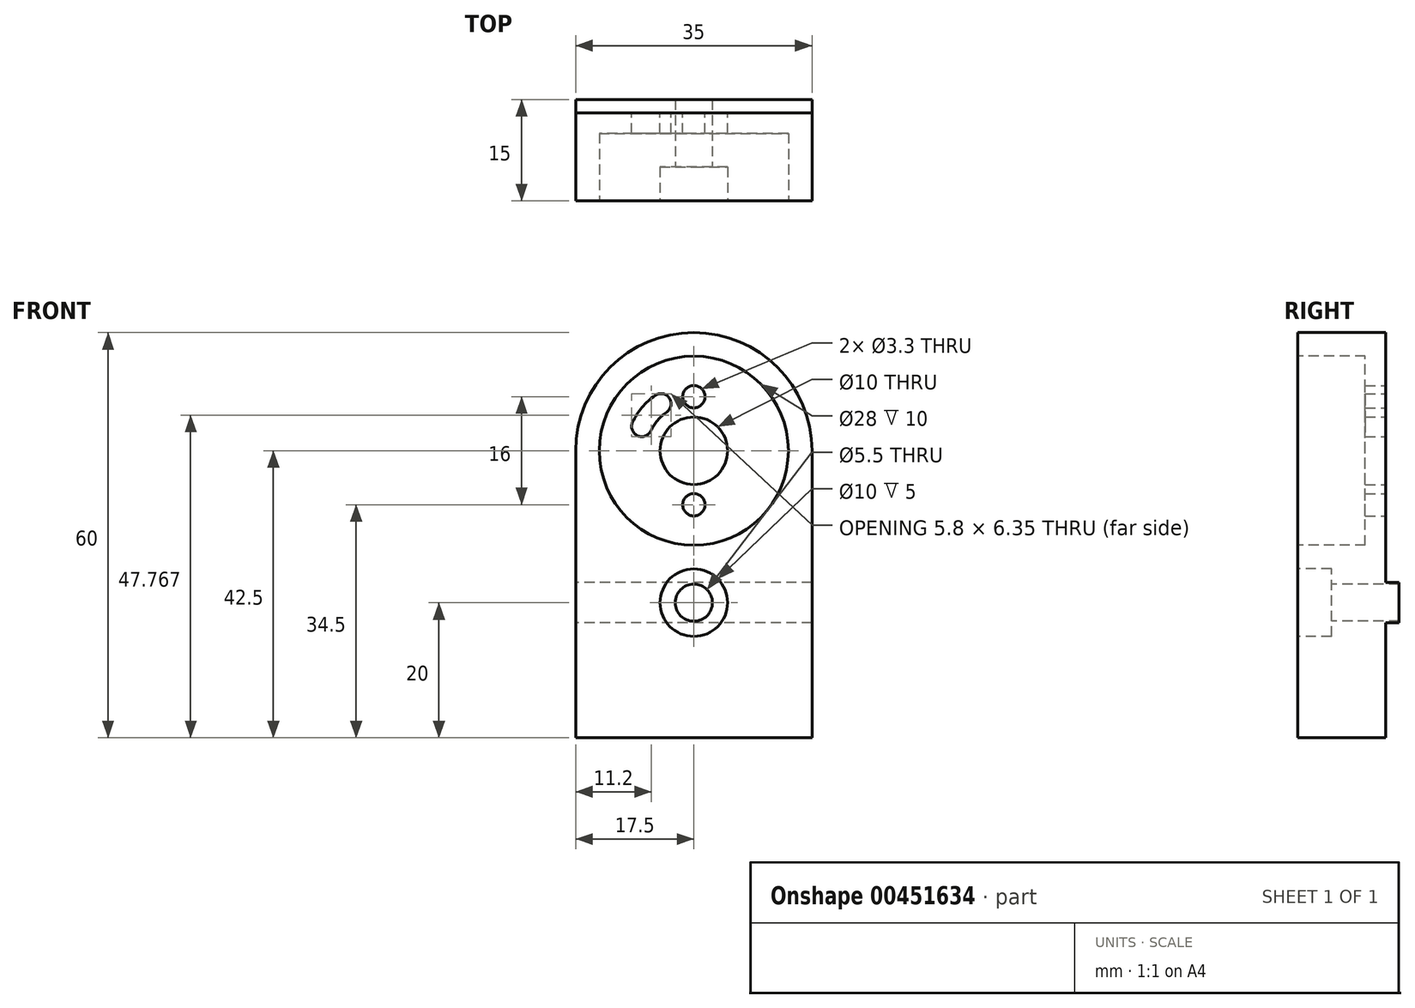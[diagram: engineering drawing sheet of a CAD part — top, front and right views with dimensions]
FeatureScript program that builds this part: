
annotation { "Feature Type Name" : "Feature", "Feature Type Description" : "" }
export const myFeature = defineFeature(function(context is Context, id is Id, definition is map)
    precondition{}
    {
        {
            var Q0;
            Q0=qCreatedBy(makeId("Front.planeOp"),FACE);
            var sketch = newSketch(context, id + "F0", { "sketchPlane" : qUnion([Q0])});
            skLineSegment(sketch, "E0.bottom", {"start": v(-17.5, 30) * mm, "end": v(17.5, 30) * mm});
            skLineSegment(sketch, "E0.top", {"start": v(-17.5, -30) * mm, "end": v(17.5, -30) * mm});
            skLineSegment(sketch, "E0.left", {"start": v(-17.5, 30) * mm, "end": v(-17.5, -30) * mm});
            skLineSegment(sketch, "E0.right", {"start": v(17.5, 30) * mm, "end": v(17.5, -30) * mm});
            skPoint(sketch, "E0.middle", {"position": v(0, 0) * mm});
            skSolve(sketch);
        }
        {
            var Q0;
            Q0 = qSketchRegion(id + "F0", true);
            extrude(context, id + "F1", {"entities" : qUnion([Q0]), "depth" : 15 * mm});
        }
        {
            var Q0;
            Q0=makeQuery(id+"F1.opExtrude","CAP_FACE",FACE,{"disambiguationData":[OSD([sQuery(id+"F0.wireOp",EDGE,"E0.bottom"),sQuery(id+"F0.wireOp",EDGE,"E0.top"),sQuery(id+"F0.wireOp",EDGE,"E0.left"),sQuery(id+"F0.wireOp",EDGE,"E0.right")])],"isStart":true});
            var sketch = newSketch(context, id + "F2", { "sketchPlane" : qUnion([Q0])});
            skCircle(sketch, "E1", {"center": v(0, 12.5) * mm, "radius": 5 * mm});
            skSolve(sketch);
        }
        {
            var Q0;
            Q0 = qSketchRegion(id + "F2", true);
            extrude(context, id + "F3", {"entities" : qUnion([Q0]), "operationType" : NewBodyOperationType.REMOVE, "oppositeDirection" : true, "depth" : 25 * mm});
        }
        {
            var Q0;
            Q0=makeQuery(id+"F1.opExtrude","SWEPT_EDGE",EDGE,{"disambiguationData":[OSD([sQuery(id+"F0.wireOp",EDGE,"E0.bottom"),sQuery(id+"F0.wireOp",EDGE,"E0.right")])]});
            var Q1;
            Q1=makeQuery(id+"F1.opExtrude","SWEPT_EDGE",EDGE,{"disambiguationData":[OSD([sQuery(id+"F0.wireOp",EDGE,"E0.bottom"),sQuery(id+"F0.wireOp",EDGE,"E0.left")])]});
            fillet(context, id + "F4", {"entities" : qUnion([Q0, Q1]), "radius" : 17.5 * mm, "tangentPropagation" : true, "allowEdgeOverflow" : false});
        }
        {
            var Q0;
            Q0=makeQuery(id+"F1.opExtrude","CAP_FACE",FACE,{"disambiguationData":[OSD([sQuery(id+"F0.wireOp",EDGE,"E0.bottom"),sQuery(id+"F0.wireOp",EDGE,"E0.top"),sQuery(id+"F0.wireOp",EDGE,"E0.left"),sQuery(id+"F0.wireOp",EDGE,"E0.right")])],"isStart":true});
            var sketch = newSketch(context, id + "F5", { "sketchPlane" : qUnion([Q0])});
            skArc(sketch, "E2", {"start": v(9.06, 16.73) * mm, "mid": v(7.66, 18.93) * mm, "end": v(5.74, 20.7) * mm});
            skArc(sketch, "E3.0", {"start": v(6.34, 15.46) * mm, "mid": v(5.36, 17) * mm, "end": v(4.02, 18.23) * mm});
            skArc(sketch, "E4", {"start": v(5.74, 20.7) * mm, "mid": v(3.65, 20.32) * mm, "end": v(4.02, 18.23) * mm});
            skArc(sketch, "E5", {"start": v(6.34, 15.46) * mm, "mid": v(8.34, 14.73) * mm, "end": v(9.06, 16.73) * mm});
            skPoint(sketch, "E6.center", {"position": v(0, 0) * mm});
            skLineSegment(sketch, "E7", {"start": v(0, 12.5) * mm, "end": v(4.88, 19.46) * mm, "construction": true});
            skLineSegment(sketch, "E8", {"start": v(0, 12.5) * mm, "end": v(0, 20.2) * mm, "construction": true});
            skSolve(sketch);
        }
        {
            var Q0;
            Q0 = qSketchRegion(id + "F5", true);
            extrude(context, id + "F6", {"entities" : qUnion([Q0]), "operationType" : NewBodyOperationType.REMOVE, "endBound" : BoundingType.THROUGH_ALL, "oppositeDirection" : true, "depth" : 25 * mm});
        }
        {
            var Q0;
            Q0=qCreatedBy(makeId("Top.planeOp"),FACE);
            cPlane(context, id + "F7", {"entities" : qUnion([Q0]), "cplaneType" : CPlaneType.OFFSET, "offset" : 12.5 * mm, "width" : 150 * mm, "height" : 150 * mm});
        }
        {
            var Q0;
            Q0=makeQuery(id+"F1.opExtrude","CAP_FACE",FACE,{"disambiguationData":[OSD([sQuery(id+"F0.wireOp",EDGE,"E0.bottom"),sQuery(id+"F0.wireOp",EDGE,"E0.top"),sQuery(id+"F0.wireOp",EDGE,"E0.left"),sQuery(id+"F0.wireOp",EDGE,"E0.right")])],"isStart":false});
            var sketch = newSketch(context, id + "F8", { "sketchPlane" : qUnion([Q0])});
            skCircle(sketch, "E9", {"center": v(0, 12.5) * mm, "radius": 14 * mm});
            skSolve(sketch);
        }
        {
            var Q0;
            Q0 = qSketchRegion(id + "F8", true);
            extrude(context, id + "F9", {"entities" : qUnion([Q0]), "operationType" : NewBodyOperationType.REMOVE, "oppositeDirection" : true, "depth" : 10 * mm});
        }
        {
            var Q0;
            Q0=qCreatedBy(makeId("Front.planeOp"),FACE);
            var sketch = newSketch(context, id + "F10", { "sketchPlane" : qUnion([Q0])});
            skArc(sketch, "E10.0", {"start": v(-17.5, 12.5) * mm, "mid": v(0, 30) * mm, "end": v(17.5, 12.5) * mm});
            skLineSegment(sketch, "E11.0", {"start": v(17.5, 12.5) * mm, "end": v(17.5, -7) * mm});
            skLineSegment(sketch, "E12.0", {"start": v(-17.5, -30) * mm, "end": v(17.5, -30) * mm});
            skLineSegment(sketch, "E13.0", {"start": v(-17.5, 12.5) * mm, "end": v(-17.5, -7) * mm});
            skLineSegment(sketch, "E14", {"start": v(17.5, -13) * mm, "end": v(-17.5, -13) * mm});
            skLineSegment(sketch, "E15.trimOffspring", {"start": v(17.5, -13) * mm, "end": v(17.5, -30) * mm});
            skLineSegment(sketch, "E16.trimOffspring", {"start": v(-17.5, -13) * mm, "end": v(-17.5, -30) * mm});
            skLineSegment(sketch, "E17", {"start": v(17.5, -7) * mm, "end": v(-17.5, -7) * mm});
            skPoint(sketch, "E18.orphan", {"position": v(17.5, -8.75) * mm});
            skPoint(sketch, "E19.orphan", {"position": v(-17.5, -8.75) * mm});
            skSolve(sketch);
        }
        {
            var Q0;
            Q0 = qSketchRegion(id + "F10", true);
            extrude(context, id + "F11", {"entities" : qUnion([Q0]), "operationType" : NewBodyOperationType.REMOVE, "depth" : 2 * mm});
        }
        {
            var Q0;
            Q0=makeQuery(id+"F1.opExtrude","CAP_FACE",FACE,{"disambiguationData":[OSD([sQuery(id+"F0.wireOp",EDGE,"E0.bottom"),sQuery(id+"F0.wireOp",EDGE,"E0.top"),sQuery(id+"F0.wireOp",EDGE,"E0.left"),sQuery(id+"F0.wireOp",EDGE,"E0.right")])],"isStart":false});
            var sketch = newSketch(context, id + "F12", { "sketchPlane" : qUnion([Q0])});
            skPoint(sketch, "E20", {"position": v(0, -10) * mm});
            skSolve(sketch);
        }
        {
            var Q0;
            Q0=sQuery(id+"F12.wireOp",VERTEX,"E20");
            var Q1;
            Q1=makeQuery(id+"F1.opExtrude","SWEPT_BODY",BODY,{"disambiguationData":[OSD([sQuery(id+"F0.wireOp",EDGE,"E0.bottom"),sQuery(id+"F0.wireOp",EDGE,"E0.top"),sQuery(id+"F0.wireOp",EDGE,"E0.left"),sQuery(id+"F0.wireOp",EDGE,"E0.right")])]});
            hole(context, id + "F13", {"style" : HoleStyle.C_BORE, "endStyle" : HoleEndStyle.THROUGH, "holeDiameter" : 5.5 * mm, "cBoreDiameter" : 10 * mm, "cBoreDepth" : 5 * mm, "isTappedThrough" : true, "tappedDepth" : 19.75 * mm, "tapClearance" : 3, "locations" : qUnion([Q0]), "scope" : qUnion([Q1])});
        }
        {
            var Q0;
            Q0=makeQuery(id+"F11.boolean.opBoolean","COPY",FACE,{"derivedFrom":makeQuery(id+"F11.opExtrude","CAP_FACE",FACE,{"disambiguationData":[OSD([sQuery(id+"F10.wireOp",EDGE,"E10.0"),sQuery(id+"F10.wireOp",EDGE,"E11.0"),sQuery(id+"F10.wireOp",EDGE,"E13.0"),sQuery(id+"F10.wireOp",EDGE,"E17")])],"isStart":false})});
            var sketch = newSketch(context, id + "F14", { "sketchPlane" : qUnion([Q0])});
            skPoint(sketch, "E21", {"position": v(0, 20.5) * mm});
            skPoint(sketch, "E22", {"position": v(0, 4.5) * mm});
            skPoint(sketch, "E23", {"position": v(0, 12.5) * mm});
            skSolve(sketch);
        }
        {
            var Q0;
            Q0=sQuery(id+"F14.wireOp",VERTEX,"E21");
            var Q1;
            Q1=sQuery(id+"F14.wireOp",VERTEX,"E22");
            var Q2;
            Q2=makeQuery(id+"F1.opExtrude","SWEPT_BODY",BODY,{"disambiguationData":[OSD([sQuery(id+"F0.wireOp",EDGE,"E0.bottom"),sQuery(id+"F0.wireOp",EDGE,"E0.top"),sQuery(id+"F0.wireOp",EDGE,"E0.left"),sQuery(id+"F0.wireOp",EDGE,"E0.right")])]});
            hole(context, id + "F15", {"style" : HoleStyle.SIMPLE, "endStyle" : HoleEndStyle.THROUGH, "holeDiameter" : 3.3 * mm, "isTappedThrough" : true, "tappedDepth" : 19.75 * mm, "tapClearance" : 3, "locations" : qUnion([Q0, Q1]), "scope" : qUnion([Q2])});
        }
    });
